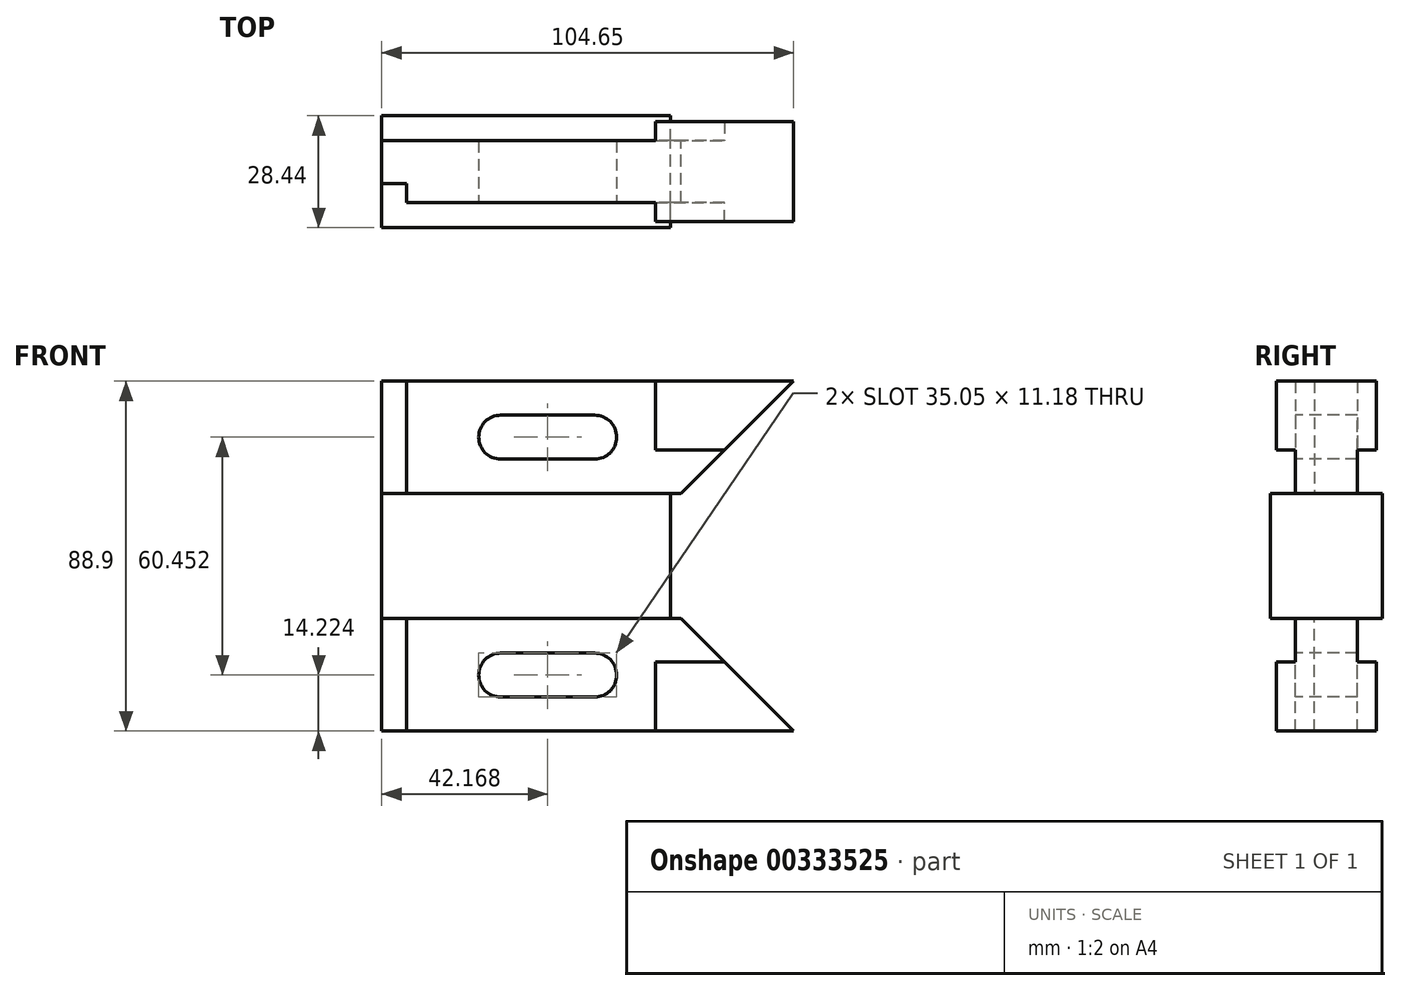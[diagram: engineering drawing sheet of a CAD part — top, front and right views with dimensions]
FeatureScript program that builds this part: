
annotation { "Feature Type Name" : "Feature", "Feature Type Description" : "" }
export const myFeature = defineFeature(function(context is Context, id is Id, definition is map)
    precondition{}
    {
        {
            var Q0;
            Q0=qCreatedBy(makeId("Front.planeOp"),FACE);
            var sketch = newSketch(context, id + "F0", { "sketchPlane" : qUnion([Q0])});
            skLineSegment(sketch, "E0", {"start": v(2.02, 44.45) * mm, "end": v(106.67, 44.45) * mm});
            skLineSegment(sketch, "E1", {"start": v(106.67, 44.45) * mm, "end": v(78.1, 15.88) * mm});
            skLineSegment(sketch, "E2", {"start": v(78.1, 15.88) * mm, "end": v(75.43, 15.88) * mm});
            skLineSegment(sketch, "E3.MirrorCS", {"start": v(2.02, -44.45) * mm, "end": v(106.67, -44.45) * mm});
            skLineSegment(sketch, "E4.MirrorCS", {"start": v(106.67, -44.45) * mm, "end": v(78.1, -15.88) * mm});
            skLineSegment(sketch, "E5.MirrorCS", {"start": v(78.1, -15.88) * mm, "end": v(75.43, -15.88) * mm});
            skPoint(sketch, "E6.start.orphan", {"position": v(0, 0) * mm});
            skPoint(sketch, "E7.MirrorCS.end.orphan", {"position": v(2.02, -44.45) * mm});
            skLineSegment(sketch, "E8", {"start": v(2.02, 44.45) * mm, "end": v(2.02, -44.45) * mm});
            skPoint(sketch, "E9.end.orphan", {"position": v(81.05, 0) * mm});
            skPoint(sketch, "E10.MirrorCS.start.orphan", {"position": v(75.43, -15.88) * mm});
            skLineSegment(sketch, "E11", {"start": v(75.43, 15.88) * mm, "end": v(75.43, -15.88) * mm});
            skSolve(sketch);
        }
        {
            var Q0;
            Q0 = qSketchRegion(id + "F0", true);
            extrude(context, id + "F1", {"entities" : qUnion([Q0]), "depth" : 28.45 * mm, "offsetDistance" : 25.4 * mm, "symmetric" : true});
        }
        {
            var Q0;
            Q0=makeQuery(id+"F1.opExtrude","SWEPT_FACE",FACE,{"disambiguationData":[OSD([sQuery(id+"F0.wireOp",EDGE,"E8")])]});
            var sketch = newSketch(context, id + "F2", { "sketchPlane" : qUnion([Q0])});
            skLineSegment(sketch, "E12.bottom", {"start": v(-14.22, 44.45) * mm, "end": v(-7.87, 44.45) * mm});
            skLineSegment(sketch, "E12.top", {"start": v(-14.22, 15.88) * mm, "end": v(-7.87, 15.88) * mm});
            skLineSegment(sketch, "E12.left", {"start": v(-14.22, 44.45) * mm, "end": v(-14.22, 15.88) * mm});
            skLineSegment(sketch, "E12.right", {"start": v(-7.87, 44.45) * mm, "end": v(-7.87, 15.88) * mm});
            skLineSegment(sketch, "E13.MirrorCS", {"start": v(14.22, 44.45) * mm, "end": v(14.22, 15.88) * mm});
            skLineSegment(sketch, "E14.MirrorCS", {"start": v(14.22, 15.88) * mm, "end": v(7.87, 15.88) * mm});
            skLineSegment(sketch, "E15.MirrorCS", {"start": v(7.87, 44.45) * mm, "end": v(7.87, 15.88) * mm});
            skLineSegment(sketch, "E16.MirrorCS", {"start": v(14.22, 44.45) * mm, "end": v(7.87, 44.45) * mm});
            skLineSegment(sketch, "E17.MirrorCS", {"start": v(-7.87, -44.45) * mm, "end": v(-7.87, -15.88) * mm});
            skLineSegment(sketch, "E18.MirrorCS", {"start": v(-14.22, -15.88) * mm, "end": v(-7.87, -15.88) * mm});
            skLineSegment(sketch, "E19.MirrorCS", {"start": v(-14.22, -44.45) * mm, "end": v(-14.22, -15.88) * mm});
            skLineSegment(sketch, "E20.MirrorCS", {"start": v(14.22, -15.88) * mm, "end": v(7.87, -15.88) * mm});
            skLineSegment(sketch, "E21.MirrorCS", {"start": v(7.87, -44.45) * mm, "end": v(7.87, -15.88) * mm});
            skLineSegment(sketch, "E22.MirrorCS", {"start": v(14.22, -44.45) * mm, "end": v(7.87, -44.45) * mm});
            skLineSegment(sketch, "E23.MirrorCS", {"start": v(14.22, -44.45) * mm, "end": v(14.22, -15.88) * mm});
            skLineSegment(sketch, "E24.MirrorCS", {"start": v(-14.22, -44.45) * mm, "end": v(-7.87, -44.45) * mm});
            skSolve(sketch);
        }
        {
            var Q0;
            Q0 = qSketchRegion(id + "F2", true);
            extrude(context, id + "F3", {"entities" : qUnion([Q0]), "operationType" : NewBodyOperationType.REMOVE, "endBound" : BoundingType.THROUGH_ALL, "oppositeDirection" : true, "depth" : 25.4 * mm, "offsetDistance" : 25.4 * mm});
        }
        {
            var Q0;
            Q0=makeQuery(id+"F3.boolean.opBoolean","COPY",FACE,{"derivedFrom":makeQuery(id+"F3.opExtrude","SWEPT_FACE",FACE,{"disambiguationData":[OSD([sQuery(id+"F2.wireOp",EDGE,"E15.MirrorCS")])]})});
            var sketch = newSketch(context, id + "F4", { "sketchPlane" : qUnion([Q0])});
            skLineSegment(sketch, "E25", {"start": v(71.62, 44.45) * mm, "end": v(71.62, 26.92) * mm});
            skLineSegment(sketch, "E26", {"start": v(71.62, 26.92) * mm, "end": v(89.15, 26.92) * mm});
            skLineSegment(sketch, "E27", {"start": v(89.15, 26.92) * mm, "end": v(106.67, 44.45) * mm});
            skLineSegment(sketch, "E28", {"start": v(106.67, 44.45) * mm, "end": v(71.62, 44.45) * mm});
            skSolve(sketch);
        }
        {
            var Q0;
            Q0 = qSketchRegion(id + "F4", true);
            extrude(context, id + "F5", {"entities" : qUnion([Q0]), "operationType" : NewBodyOperationType.ADD, "depth" : 4.83 * mm, "offsetDistance" : 25.4 * mm});
        }
        {
            var Q0;
            Q0=makeQuery(id+"F1.opExtrude","SWEPT_BODY",BODY,{"disambiguationData":[OSD([sQuery(id+"F0.wireOp",EDGE,"E0"),sQuery(id+"F0.wireOp",EDGE,"E1"),sQuery(id+"F0.wireOp",EDGE,"E2"),sQuery(id+"F0.wireOp",EDGE,"E3.MirrorCS"),sQuery(id+"F0.wireOp",EDGE,"E4.MirrorCS"),sQuery(id+"F0.wireOp",EDGE,"E5.MirrorCS"),sQuery(id+"F0.wireOp",EDGE,"E8"),sQuery(id+"F0.wireOp",EDGE,"E11")])]});
            var Q1;
            Q1=qCreatedBy(makeId("Front.planeOp"),FACE);
            mirror(context, id + "F6", {"operationType" : NewBodyOperationType.ADD, "entities" : qUnion([Q0]), "mirrorPlane" : qUnion([Q1])});
        }
        {
            var Q0;
            Q0=makeQuery(id+"F1.opExtrude","SWEPT_BODY",BODY,{"disambiguationData":[OSD([sQuery(id+"F0.wireOp",EDGE,"E0"),sQuery(id+"F0.wireOp",EDGE,"E1"),sQuery(id+"F0.wireOp",EDGE,"E2"),sQuery(id+"F0.wireOp",EDGE,"E3.MirrorCS"),sQuery(id+"F0.wireOp",EDGE,"E4.MirrorCS"),sQuery(id+"F0.wireOp",EDGE,"E5.MirrorCS"),sQuery(id+"F0.wireOp",EDGE,"E8"),sQuery(id+"F0.wireOp",EDGE,"E11")])]});
            var Q1;
            Q1=qCreatedBy(makeId("Top.planeOp"),FACE);
            mirror(context, id + "F7", {"operationType" : NewBodyOperationType.ADD, "entities" : qUnion([Q0]), "mirrorPlane" : qUnion([Q1])});
        }
        {
            var Q0;
            Q0=makeQuery(id+"F1.opExtrude","SWEPT_FACE",FACE,{"disambiguationData":[OSD([sQuery(id+"F0.wireOp",EDGE,"E8")])]});
            var sketch = newSketch(context, id + "F8", { "sketchPlane" : qUnion([Q0])});
            skLineSegment(sketch, "E29.bottom", {"start": v(7.87, 44.45) * mm, "end": v(3.05, 44.45) * mm});
            skLineSegment(sketch, "E29.top", {"start": v(7.87, 15.88) * mm, "end": v(3.05, 15.88) * mm});
            skLineSegment(sketch, "E29.left", {"start": v(7.87, 44.45) * mm, "end": v(7.87, 15.88) * mm});
            skLineSegment(sketch, "E29.right", {"start": v(3.05, 44.45) * mm, "end": v(3.05, 15.88) * mm});
            skLineSegment(sketch, "E30.bottom", {"start": v(7.87, -44.45) * mm, "end": v(3.05, -44.45) * mm});
            skLineSegment(sketch, "E30.top", {"start": v(7.87, -15.88) * mm, "end": v(3.05, -15.88) * mm});
            skLineSegment(sketch, "E30.left", {"start": v(7.87, -44.45) * mm, "end": v(7.87, -15.88) * mm});
            skLineSegment(sketch, "E30.right", {"start": v(3.05, -44.45) * mm, "end": v(3.05, -15.88) * mm});
            skSolve(sketch);
        }
        {
            var Q0;
            Q0 = qSketchRegion(id + "F8", true);
            extrude(context, id + "F9", {"entities" : qUnion([Q0]), "operationType" : NewBodyOperationType.REMOVE, "oppositeDirection" : true, "depth" : 6.35 * mm, "offsetDistance" : 25.4 * mm});
        }
        {
            var Q0;
            Q0=makeQuery(id+"F3.boolean.opBoolean","COPY",FACE,{"derivedFrom":makeQuery(id+"F3.opExtrude","SWEPT_FACE",FACE,{"disambiguationData":[OSD([sQuery(id+"F2.wireOp",EDGE,"E21.MirrorCS")])]})});
            var sketch = newSketch(context, id + "F10", { "sketchPlane" : qUnion([Q0])});
            skLineSegment(sketch, "E31", {"start": v(-23.76, -30.23) * mm, "end": v(111.7, -30.23) * mm, "construction": true});
            skLineSegment(sketch, "E32", {"start": v(26.66, -18.87) * mm, "end": v(26.66, -55.15) * mm, "construction": true});
            skLineSegment(sketch, "E33", {"start": v(61.71, -20.42) * mm, "end": v(61.71, -56.24) * mm, "construction": true});
            skLineSegment(sketch, "E34", {"start": v(44.19, -18.52) * mm, "end": v(44.19, -48.37) * mm, "construction": true});
            skArc(sketch, "E35", {"start": v(32.25, -24.64) * mm, "mid": v(26.66, -30.23) * mm, "end": v(32.25, -35.81) * mm});
            skArc(sketch, "E36.MirrorC", {"start": v(56.13, -24.64) * mm, "mid": v(61.71, -30.23) * mm, "end": v(56.13, -35.81) * mm});
            skLineSegment(sketch, "E37", {"start": v(32.25, -30.23) * mm, "end": v(32.25, -24.64) * mm, "construction": true});
            skLineSegment(sketch, "E38", {"start": v(32.25, -24.64) * mm, "end": v(32.25, -35.81) * mm, "construction": true});
            skPoint(sketch, "E38.endSnap0", {"position": v(32.25, -27.43) * mm});
            skLineSegment(sketch, "E39", {"start": v(56.13, -30.23) * mm, "end": v(56.13, -24.64) * mm, "construction": true});
            skLineSegment(sketch, "E40", {"start": v(56.13, -24.64) * mm, "end": v(56.13, -35.81) * mm, "construction": true});
            skLineSegment(sketch, "E41", {"start": v(56.13, -35.81) * mm, "end": v(32.25, -35.81) * mm});
            skLineSegment(sketch, "E42", {"start": v(32.25, -24.64) * mm, "end": v(56.13, -24.64) * mm});
            skLineSegment(sketch, "E43.MirrorCS", {"start": v(32.25, 24.64) * mm, "end": v(56.13, 24.64) * mm});
            skArc(sketch, "E44.MirrorCS", {"start": v(32.25, 24.64) * mm, "mid": v(26.66, 30.23) * mm, "end": v(32.25, 35.81) * mm});
            skLineSegment(sketch, "E45.MirrorCS", {"start": v(56.13, 35.81) * mm, "end": v(32.25, 35.81) * mm});
            skLineSegment(sketch, "E46.MirrorCS", {"start": v(61.71, 20.42) * mm, "end": v(61.71, 56.24) * mm, "construction": true});
            skArc(sketch, "E47.MirrorCS", {"start": v(56.13, 24.64) * mm, "mid": v(61.71, 30.23) * mm, "end": v(56.13, 35.81) * mm});
            skSolve(sketch);
        }
        {
            var Q0;
            Q0 = qSketchRegion(id + "F10", true);
            extrude(context, id + "F11", {"entities" : qUnion([Q0]), "operationType" : NewBodyOperationType.REMOVE, "endBound" : BoundingType.THROUGH_ALL, "oppositeDirection" : true, "depth" : 25.4 * mm, "offsetDistance" : 25.4 * mm});
        }
    });
